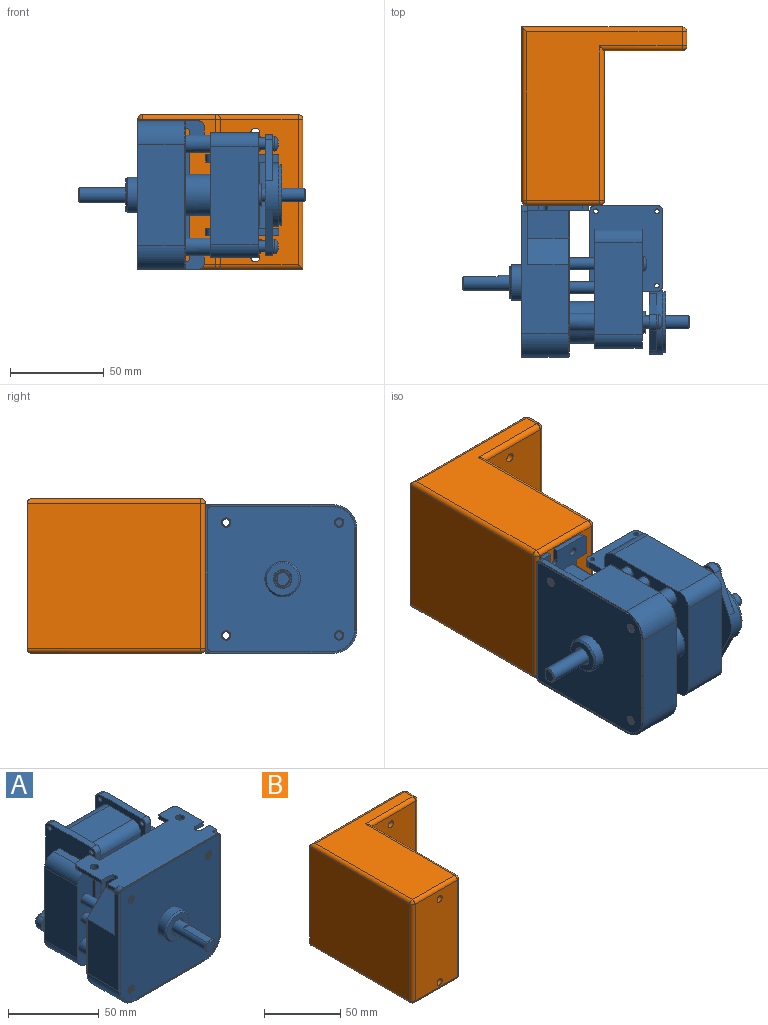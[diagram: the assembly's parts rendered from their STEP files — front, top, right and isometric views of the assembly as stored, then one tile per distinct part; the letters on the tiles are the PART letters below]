
ASSEMBLY  parts=2 mates=1
PART A: 196 faces, bbox 81.7x121.6x82.2 mm
  f0: plane 35.26x18.4mm, normal (0,0,-1), area 648.6mm2, adj f167,f168,f174,f176
  f1: plane 35.26x18.4mm, normal (0,0,1), area 648.6mm2, adj f167,f168,f175,f177
  f2: plane 39.76x3.96mm, normal (0,-1,0), area 157.5mm2, adj f165,f167,f179,f181
  f3: plane 39.69x3.96mm, normal (0,1,0), area 157.3mm2, adj f165,f167,f182,f185
  f4: plane 35.26x25.4mm, normal (0,0,1), area 895.5mm2, adj f6,f106,f167,f168
  f5: plane 78.11x77.78mm, normal (0,1,0), area 4716.9mm2, adj f72,f96,f97,f98,f99,f100,f101,f102
  f6: plane 66.68x63.5mm, normal (0,-1,0), area 2092.8mm2, adj f4,f105,f108,f109,f110,f111,f112,f113
  f7: plane 9.46x2.54mm, normal (0,1,0), area 24mm2, adj f12,f72,f92,f94
  f8: plane 5.54x2.54mm, normal (-1,0,0), area 14.1mm2, adj f12,f72,f78,f88
  f9: plane 5.54x2.54mm, normal (1,0,0), area 14.1mm2, adj f12,f72,f79,f83
  f10: plane 78.66x77.09mm, normal (0,-1,0), area 5641.5mm2, adj f29,f30,f31,f32,f33,f34,f35,f36
  f11: cylinder r=3.17mm len=3.18mm, axis (0,-1,0), area 15.8mm2, adj f12,f18,f19,f75,f78
  f12: plane 79.25x35.56mm, normal (0,0,1), area 2254.7mm2, adj f7,f8,f9,f11,f13,f19,f78,f79
  f13: cylinder r=3.17mm len=3.18mm, axis (0,-1,0), area 15.8mm2, adj f12,f14,f19,f71,f79
  f14: plane 65.08x24.77mm, normal (1,0,0), area 994.6mm2, adj f13,f15,f19,f71,f73,f104
  f15: cylinder r=12.7mm len=24.77mm, axis (0,-1,0), area 494mm2, adj f14,f16,f19,f102
  f16: plane 53.98x24.77mm, normal (0,0,-1), area 1336.7mm2, adj f15,f17,f19,f100
  f17: cylinder r=12.7mm len=24.77mm, axis (0,-1,0), area 494mm2, adj f16,f18,f19,f99
  f18: plane 65.08x24.77mm, normal (-1,0,0), area 994.6mm2, adj f11,f17,f19,f75,f77,f98
  f19: plane 80.95x79.38mm, normal (0,-1,0), area 270.5mm2, adj f11,f12,f13,f14,f15,f16,f17,f18
  f20: cylinder r=2.29mm len=2.29mm, axis (0,-1,0), area 2.7mm2, adj f19,f21,f27,f28
  f21: plane 73.03x0.76mm, normal (0,0,-1), area 55.6mm2, adj f19,f20,f22,f28
  f22: cylinder r=2.29mm len=2.29mm, axis (0,-1,0), area 2.7mm2, adj f19,f21,f23,f28
  f23: plane 65.08x0.76mm, normal (-1,0,0), area 49.6mm2, adj f19,f22,f24,f28
  f24: cylinder r=11.81mm len=11.81mm, axis (0,-1,0), area 14.1mm2, adj f19,f23,f25,f28
  f25: plane 53.98x0.76mm, normal (0,0,1), area 41.1mm2, adj f19,f24,f26,f28
  f26: cylinder r=11.81mm len=11.81mm, axis (0,-1,0), area 14.1mm2, adj f19,f25,f27,f28
  f27: plane 65.08x0.76mm, normal (1,0,0), area 49.6mm2, adj f19,f20,f26,f28
  f28: plane 79.17x77.6mm, normal (0,-1,0), area 76.4mm2, adj f20,f21,f22,f23,f24,f25,f26,f27
  f29: cylinder r=2.03mm len=2.03mm, axis (0,-1,0), area 2.4mm2, adj f10,f28,f30,f36
  f30: plane 73.03x0.76mm, normal (0,0,1), area 55.6mm2, adj f10,f28,f29,f31
  f31: cylinder r=2.03mm len=2.03mm, axis (0,-1,0), area 2.4mm2, adj f10,f28,f30,f32
  f32: plane 65.08x0.76mm, normal (1,0,0), area 49.6mm2, adj f10,f28,f31,f33
  f33: cylinder r=11.56mm len=11.56mm, axis (0,-1,0), area 13.8mm2, adj f10,f28,f32,f34
  f34: plane 53.98x0.76mm, normal (0,0,-1), area 41.1mm2, adj f10,f28,f33,f35
  f35: cylinder r=11.56mm len=11.56mm, axis (0,-1,0), area 13.8mm2, adj f10,f28,f34,f36
  f36: plane 65.08x0.76mm, normal (-1,0,0), area 49.6mm2, adj f10,f28,f29,f35
  f37: cylinder r=9.53mm len=19.05mm, axis (0,1,0), area 326.8mm2, adj f10,f61
  f38: plane 17.27x17.27mm, normal (0,-1,0), area 156.2mm2, adj f61,f65
  f39: cone r=2.5mm half-angle=45deg, axis (0,-1,0), area 6.7mm2, adj f10,f41,f42,f43,f44
  f40: plane 4.62x4.56mm, normal (0,-1,0), area 14.9mm2, adj f41,f42,f43,f44
  f41: cylinder r=2.41mm len=6.26mm, axis (0,-1,0), area 6.6mm2, adj f39,f40,f42,f44
  f42: bspline ~6.76x5.67mm, area 52.2mm2, adj f39,f40,f41,f43
  f43: cylinder r=1.98mm len=5.83mm, axis (0,1,0), area 10.7mm2, adj f39,f40,f42,f44
  f44: bspline ~6.89x5.67mm, area 51.4mm2, adj f39,f40,f41,f43
  f45: cone r=2.5mm half-angle=45deg, axis (0,-1,0), area 6.7mm2, adj f10,f47,f48,f49,f50
  f46: plane 4.62x4.56mm, normal (0,-1,0), area 14.9mm2, adj f47,f48,f49,f50
  f47: cylinder r=2.41mm len=6.26mm, axis (0,-1,0), area 6.6mm2, adj f45,f46,f48,f50
  f48: bspline ~6.76x5.67mm, area 52.2mm2, adj f45,f46,f47,f49
  f49: cylinder r=1.98mm len=5.83mm, axis (0,1,0), area 10.7mm2, adj f45,f46,f48,f50
  f50: bspline ~6.89x5.67mm, area 51.4mm2, adj f45,f46,f47,f49
  f51: cone r=2.5mm half-angle=45deg, axis (0,-1,0), area 6.7mm2, adj f10,f52,f53,f54,f55
  f52: cylinder r=2.41mm len=4.83mm, axis (0,-1,0), area 6.1mm2, adj f51,f53,f55,f75
  f53: bspline ~5.67x4.91mm, area 24.9mm2, adj f51,f52,f54,f75
  f54: cylinder r=1.98mm len=3.97mm, axis (0,1,0), area 8.3mm2, adj f51,f53,f55,f75
  f55: bspline ~5.67x4.91mm, area 24.2mm2, adj f51,f52,f54,f75
  f56: cone r=2.5mm half-angle=45deg, axis (0,-1,0), area 6.7mm2, adj f10,f57,f58,f59,f60
  f57: cylinder r=2.41mm len=4.83mm, axis (0,-1,0), area 6.1mm2, adj f56,f58,f60,f71
  f58: bspline ~5.67x4.91mm, area 24.9mm2, adj f56,f57,f59,f71
  f59: cylinder r=1.98mm len=3.97mm, axis (0,1,0), area 8.3mm2, adj f56,f58,f60,f71
  f60: bspline ~5.67x4.91mm, area 24.2mm2, adj f56,f57,f59,f71
  f61: cone r=8.64mm half-angle=45deg, axis (0,1,0), area 71.7mm2, adj f37,f38
  f62: cylinder r=4.6mm len=9.21mm, axis (0,-1,0), area 33.1mm2, adj f63,f65
  f63: plane 9.21x9.21mm, normal (0,-1,0), area 17.1mm2, adj f62,f64
  f64: cylinder r=3.97mm len=26.42mm, axis (0,-1,0), area 563.9mm2, adj f63,f67,f68,f70
  f65: cone r=4.6mm half-angle=45deg, axis (0,-1,0), area 16.2mm2, adj f38,f62
  f66: plane 6.92x6.13mm, normal (0,-1,0), area 35.2mm2, adj f69,f70
  f67: plane 18.54x4.77mm, normal (0,0,1), area 88.4mm2, adj f64,f68,f69
  f68: plane 4.77x0.8mm, normal (0,-1,0), area 2.6mm2, adj f64,f67
  f69: plane 4.78x0.52mm, normal (0,-0.71,0.71), area 3.3mm2, adj f66,f67,f70
  f70: cone r=3.46mm half-angle=45deg, axis (0,1,0), area 13.2mm2, adj f64,f66,f69
  f71: plane 29.43x14.51mm, normal (0,1,0), area 300.4mm2, adj f13,f14,f57,f58,f59,f60,f72,f73
  f72: plane 79.25x32.39mm, normal (0,0,-1), area 894mm2, adj f5,f7,f8,f9,f71,f74,f75,f76
  f73: plane 21.59x14.29mm, normal (0.71,0,0.71), area 436.2mm2, adj f14,f71,f74,f103
  f74: plane 21.59x14.92mm, normal (1,0,0), area 322.2mm2, adj f71,f72,f73,f101
  f75: plane 29.43x14.51mm, normal (0,1,0), area 300.4mm2, adj f11,f18,f52,f53,f54,f55,f72,f76
  f76: plane 21.59x14.92mm, normal (-1,0,0), area 322.2mm2, adj f72,f75,f77,f96
  f77: plane 21.59x14.29mm, normal (-0.71,0,0.71), area 436.2mm2, adj f18,f75,f76,f97
  f78: plane 3.11x2.54mm, normal (0,-1,0), area 2mm2, adj f8,f11,f12
  f79: plane 3.11x2.54mm, normal (0,-1,0), area 2mm2, adj f9,f12,f13
  f80: plane 18.9x2.54mm, normal (1,0,0), area 48mm2, adj f12,f72,f85,f94
  f81: plane 18.9x2.54mm, normal (-1,0,0), area 48mm2, adj f12,f72,f89,f95
  f82: plane 9.46x2.54mm, normal (0,1,0), area 24mm2, adj f12,f72,f93,f95
  f83: plane 6.29x2.54mm, normal (0,1,0), area 16mm2, adj f9,f12,f72,f84
  f84: cylinder r=2.38mm len=4.76mm, axis (0,0,1), area 19mm2, adj f12,f72,f83,f85
  f85: plane 6.29x2.54mm, normal (0,-1,0), area 16mm2, adj f12,f72,f80,f84
  f86: cylinder r=2.41mm len=4.83mm, axis (0,0,1), area 38.5mm2, adj f12,f72
  f87: cylinder r=2.38mm len=4.76mm, axis (0,0,1), area 19mm2, adj f12,f72,f88,f89
  f88: plane 6.29x2.54mm, normal (0,1,0), area 16mm2, adj f8,f12,f72,f87
  f89: plane 6.29x2.54mm, normal (0,-1,0), area 16mm2, adj f12,f72,f81,f87
  f90: cylinder r=2.41mm len=4.83mm, axis (0,0,1), area 38.5mm2, adj f12,f72
  f91: plane 53.98x2.54mm, normal (0,1,0), area 137.1mm2, adj f12,f72,f92,f93
  f92: plane 7.87x2.54mm, normal (-1,0,0), area 20mm2, adj f7,f12,f72,f91
  f93: plane 7.87x2.54mm, normal (1,0,0), area 20mm2, adj f12,f72,f82,f91
  f94: cylinder r=3.17mm len=3.18mm, axis (0,0,-1), area 12.7mm2, adj f7,f12,f72,f80
  f95: cylinder r=3.17mm len=3.18mm, axis (0,0,1), area 12.7mm2, adj f12,f72,f81,f82
  f96: cylinder r=0.64mm len=15.19mm, axis (0,0,-1), area 15mm2, adj f5,f72,f76,f97
  f97: cylinder r=0.64mm len=14.92mm, axis (-0.71,0,-0.71), area 20.2mm2, adj f5,f77,f96,f98
  f98: cylinder r=0.64mm len=36.5mm, axis (0,0,1), area 36.3mm2, adj f5,f18,f97,f99
  f99: torus R=12.06mm, axis (0,-1,0), area 19.5mm2, adj f5,f17,f98,f100
  f100: cylinder r=0.64mm len=53.98mm, axis (-1,0,0), area 53.8mm2, adj f5,f16,f99,f102
  f101: cylinder r=0.64mm len=15.19mm, axis (0,0,1), area 15mm2, adj f5,f72,f74,f103
  f102: torus R=12.06mm, axis (0,-1,0), area 19.5mm2, adj f5,f15,f100,f104
  f103: cylinder r=0.64mm len=14.92mm, axis (-0.71,0,0.71), area 20.2mm2, adj f5,f73,f101,f104
  f104: cylinder r=0.64mm len=36.5mm, axis (0,0,-1), area 36.3mm2, adj f5,f14,f102,f103
  f105: cylinder r=11.11mm len=22.23mm, axis (0,1,0), area 939.9mm2, adj f5,f6
  f106: plane 66.68x63.5mm, normal (0,1,0), area 2425.6mm2, adj f4,f108,f109,f110,f111,f112,f113,f114
  f107: plane 64.45x34.01mm, normal (0,-1,0), area 1284.3mm2, adj f117,f120,f121,f122,f123,f124,f125,f129
  f108: cylinder r=7.15mm len=25.4mm, axis (0,-1,0), area 285.3mm2, adj f6,f106,f109,f116
  f109: plane 49.2x25.4mm, normal (1,0,0), area 1249.7mm2, adj f6,f106,f108,f110
  f110: cylinder r=7.15mm len=25.4mm, axis (0,-1,0), area 285.3mm2, adj f6,f106,f109,f111
  f111: plane 52.38x25.4mm, normal (0,0,-1), area 1330.3mm2, adj f6,f106,f110,f112
  f112: cylinder r=7.15mm len=25.4mm, axis (0,-1,0), area 285.3mm2, adj f6,f106,f111,f113
  f113: plane 49.2x25.4mm, normal (-1,0,0), area 1249.7mm2, adj f6,f106,f112,f114
  f114: cylinder r=7.15mm len=25.4mm, axis (0,-1,0), area 285.3mm2, adj f6,f106,f113,f115
  f115: plane 25.4x4.6mm, normal (0,0,1), area 116.8mm2, adj f6,f106,f114,f163
  f116: plane 25.4x4.6mm, normal (0,0,1), area 116.8mm2, adj f6,f106,f108,f165
  f117: cylinder r=3.17mm len=6.35mm, axis (0,-1,0), area 76mm2, adj f106,f107
  f118: plane 30.44x24.65mm, normal (0,1,0), area 190.2mm2, adj f120,f121,f122,f129,f138
  f119: plane 30.44x24.65mm, normal (0,1,0), area 190.2mm2, adj f123,f124,f125,f129,f136
  f120: plane 22.01x10.96mm, normal (0.45,0,0.9), area 101.5mm2, adj f107,f118,f121,f129
  f121: cylinder r=4.76mm len=8.53mm, axis (0,1,0), area 43.6mm2, adj f107,f118,f120,f122
  f122: plane 22.01x10.96mm, normal (0.45,0,-0.9), area 101.5mm2, adj f107,f118,f121,f129
  f123: plane 22.01x10.96mm, normal (-0.45,0,0.9), area 101.5mm2, adj f107,f119,f125,f129
  f124: plane 22.01x10.96mm, normal (-0.45,0,-0.9), area 101.5mm2, adj f107,f119,f125,f129
  f125: cylinder r=4.76mm len=8.53mm, axis (0,1,0), area 43.6mm2, adj f107,f119,f123,f124
  f126: plane 32.39x32.39mm, normal (0,1,0), area 764.6mm2, adj f128,f135
  f127: plane 34.01x34.01mm, normal (0,1,0), area 84.8mm2, adj f128,f129
  f128: cylinder r=16.19mm len=32.39mm, axis (0,1,0), area 161.5mm2, adj f126,f127
  f129: cylinder r=17.01mm len=34.01mm, axis (0,1,0), area 469mm2, adj f107,f118,f119,f120,f122,f123,f124,f127
  f130: cylinder r=3.83mm len=7.66mm, axis (0,1,0), area 64.2mm2, adj f131,f135
  f131: plane 7.66x7.66mm, normal (0,1,0), area 5.9mm2, adj f130,f134
  f132: plane 6.13x6.13mm, normal (0,1,0), area 29.6mm2, adj f133
  f133: cone r=3.58mm half-angle=45deg, axis (0,-1,0), area 15mm2, adj f132,f134
  f134: cylinder r=3.58mm len=15.37mm, axis (0,1,0), area 345.2mm2, adj f131,f133
  f135: cone r=3.83mm half-angle=45deg, axis (0,1,0), area 18.4mm2, adj f126,f130
  f136: cylinder r=3.97mm len=7.94mm, axis (0,-1,0), area 19.8mm2, adj f119,f137
  f137: revolved ~7.94x7.94mm, area 70.7mm2, adj f136
  f138: cylinder r=3.97mm len=7.94mm, axis (0,-1,0), area 19.8mm2, adj f118,f139
  f139: revolved ~7.94x7.94mm, area 70.7mm2, adj f138
  f140: cylinder r=3.17mm len=6.35mm, axis (0,-1,0), area 76mm2, adj f106,f107
  f141: cylinder r=3.58mm len=7.15mm, axis (0,-1,0), area 49.9mm2, adj f107,f142
  f142: plane 11.98x11.98mm, normal (0,1,0), area 72.5mm2, adj f141,f143
  f143: cylinder r=5.99mm len=11.98mm, axis (0,-1,0), area 59.7mm2, adj f106,f142
  f144: cylinder r=1.98mm len=3.96mm, axis (0,1,0), area 11.1mm2, adj f106,f145
  f145: plane 3.96x3.96mm, normal (0,1,0), area 12.3mm2, adj f144
  f146: cylinder r=1.98mm len=3.96mm, axis (0,1,0), area 11.1mm2, adj f106,f147
  f147: plane 3.96x3.96mm, normal (0,1,0), area 12.3mm2, adj f146
  f148: cylinder r=1.98mm len=3.96mm, axis (0,1,0), area 11.1mm2, adj f106,f149
  f149: plane 3.96x3.96mm, normal (0,1,0), area 12.3mm2, adj f148
  f150: cylinder r=1.98mm len=3.96mm, axis (0,1,0), area 11.1mm2, adj f106,f151
  f151: plane 3.96x3.96mm, normal (0,1,0), area 12.3mm2, adj f150
  f152: cylinder r=3.97mm len=7.94mm, axis (0,-1,0), area 15.8mm2, adj f106,f153
  f153: revolved ~7.94x7.94mm, area 67.2mm2, adj f152
  f154: cylinder r=3.97mm len=7.94mm, axis (0,-1,0), area 15.8mm2, adj f106,f155
  f155: revolved ~7.94x7.94mm, area 67.2mm2, adj f154
  f156: cylinder r=3.17mm len=13.46mm, axis (0,1,0), area 268.6mm2, adj f5,f6
  f157: cylinder r=3.17mm len=13.46mm, axis (0,1,0), area 268.6mm2, adj f5,f6
  f158: cylinder r=4.76mm len=13.46mm, axis (0,1,0), area 402.8mm2, adj f5,f6
  f159: cylinder r=4.76mm len=13.46mm, axis (0,1,0), area 402.8mm2, adj f5,f6
  f160: cylinder r=3.17mm len=13.46mm, axis (0,1,0), area 268.6mm2, adj f5,f6
  f161: cylinder r=3.17mm len=13.46mm, axis (0,1,0), area 268.6mm2, adj f5,f6
  f162: plane 7.94x3.96mm, normal (0,0,-1), area 31.5mm2, adj f106,f163,f168,f183
  f163: plane 46.04x39.02mm, normal (-1,0,0), area 924.7mm2, adj f6,f106,f115,f162,f169,f170,f171,f178
  f164: plane 7.94x3.96mm, normal (0,0,-1), area 31.5mm2, adj f106,f165,f167,f182
  f165: plane 46.04x39.02mm, normal (1,0,0), area 924.7mm2, adj f2,f3,f6,f106,f116,f164,f166,f179
  f166: plane 32.67x3.96mm, normal (0,0,1), area 129.5mm2, adj f165,f167,f181,f185
  f167: plane 46.04x39.02mm, normal (-1,0,0), area 617.2mm2, adj f0,f1,f2,f3,f4,f164,f166,f172
  f168: plane 46.04x39.02mm, normal (1,0,0), area 617.2mm2, adj f0,f1,f4,f162,f169,f170,f171,f172
  f169: plane 32.67x3.96mm, normal (0,0,1), area 129.5mm2, adj f163,f168,f180,f184
  f170: plane 39.76x3.96mm, normal (0,-1,0), area 157.5mm2, adj f163,f168,f178,f180
  f171: plane 39.69x3.96mm, normal (0,1,0), area 157.3mm2, adj f163,f168,f183,f184
  f172: plane 35.26x25.41mm, normal (0,1,0), area 895.9mm2, adj f167,f168,f176,f177
  f173: plane 35.26x25.41mm, normal (0,-1,0), area 895.9mm2, adj f167,f168,f174,f175
  f174: cylinder r=6.35mm len=35.26mm, axis (-1,0,0), area 351.7mm2, adj f0,f167,f168,f173
  f175: cylinder r=6.35mm len=35.26mm, axis (1,0,0), area 351.7mm2, adj f1,f167,f168,f173
  f176: cylinder r=6.35mm len=35.26mm, axis (1,0,0), area 351.7mm2, adj f0,f167,f168,f172
  f177: cylinder r=6.35mm len=35.26mm, axis (-1,0,0), area 351.7mm2, adj f1,f167,f168,f172
  f178: cylinder r=3.17mm len=3.96mm, axis (-1,0,0), area 17.1mm2, adj f6,f163,f168,f170
  f179: cylinder r=3.17mm len=3.96mm, axis (-1,0,0), area 17.1mm2, adj f2,f6,f165,f167
  f180: cylinder r=3.17mm len=3.96mm, axis (-1,0,0), area 19.8mm2, adj f163,f168,f169,f170
  f181: cylinder r=3.17mm len=3.96mm, axis (-1,0,0), area 19.8mm2, adj f2,f165,f166,f167
  f182: cylinder r=3.17mm len=3.96mm, axis (1,0,0), area 19.8mm2, adj f3,f164,f165,f167
  f183: cylinder r=3.17mm len=3.96mm, axis (1,0,0), area 19.8mm2, adj f162,f163,f168,f171
  f184: cylinder r=3.17mm len=3.96mm, axis (-1,0,0), area 19.8mm2, adj f163,f168,f169,f171
  f185: cylinder r=3.17mm len=3.96mm, axis (-1,0,0), area 19.8mm2, adj f3,f165,f166,f167
  f186: cylinder r=1.27mm len=3.96mm, axis (-1,0,0), area 31.6mm2, adj f163,f168
  f187: cylinder r=1.27mm len=3.96mm, axis (-1,0,0), area 31.6mm2, adj f165,f167
  f188: cylinder r=1.27mm len=3.96mm, axis (-1,0,0), area 31.6mm2, adj f163,f168,f189
  f189: plane 2.54x1.94mm, normal (1,0,0), area 4.1mm2, adj f6,f188
  f190: plane 2.54x1.94mm, normal (-1,0,0), area 4.1mm2, adj f6,f191
  f191: cylinder r=1.27mm len=3.96mm, axis (-1,0,0), area 31.6mm2, adj f165,f167,f190
  f192: cylinder r=1.27mm len=3.96mm, axis (-1,0,0), area 31.6mm2, adj f163,f168
  f193: cylinder r=1.27mm len=3.96mm, axis (-1,0,0), area 31.6mm2, adj f165,f167
  f194: cylinder r=1.27mm len=3.96mm, axis (-1,0,0), area 31.6mm2, adj f163,f168
  f195: cylinder r=1.27mm len=3.96mm, axis (-1,0,0), area 31.6mm2, adj f165,f167
PART B: 35 faces, bbox 88.2x95.3x82.6 mm
  f0: plane 85.67x77.47mm, normal (0,1,0), area 6600.6mm2, adj f5,f8,f9,f12,f33,f34
  f1: plane 77.47x41.57mm, normal (0,-1,0), area 3183.6mm2, adj f7,f14,f23,f26,f33,f34
  f2: plane 77.47x39.03mm, normal (0,-1,0), area 2986.8mm2, adj f17,f18,f24,f25,f29,f31
  f3: plane 90.17x83.13mm, normal (0,0,1), area 3855.2mm2, adj f8,f10,f14,f15,f18,f19
  f4: plane 80.01x7.62mm, normal (1,0,0), area 609.7mm2, adj f6,f9,f15,f23
  f5: plane 92.71x77.47mm, normal (-1,0,0), area 7182.2mm2, adj f0,f10,f16,f17
  f6: plane 90.17x85.67mm, normal (0,0,-1), area 3874.5mm2, adj f4,f12,f16,f24,f26,f28
  f7: plane 80.01x77.47mm, normal (1,0,0), area 6198.4mm2, adj f1,f19,f25,f28
  f8: cylinder r=2.54mm len=85.67mm, axis (-1,0,0), area 338.1mm2, adj f0,f3,f10,f11
  f9: cylinder r=2.54mm len=80.01mm, axis (0,0,1), area 315.5mm2, adj f0,f4,f11,f12
  f10: cylinder r=2.54mm len=92.71mm, axis (0,1,0), area 366.2mm2, adj f3,f5,f8,f13
  f11: sphere r=2.54mm, area 10.1mm2, adj f8,f9,f15
  f12: cylinder r=2.54mm len=88.21mm, axis (1,0,0), area 344.6mm2, adj f0,f6,f9,f16
  f13: sphere r=2.54mm, area 10.1mm2, adj f10,f17,f18
  f14: cylinder r=2.54mm len=44.11mm, axis (1,0,0), area 169.5mm2, adj f1,f3,f19,f20
  f15: cylinder r=2.54mm len=7.62mm, axis (0,-1,0), area 30.4mm2, adj f3,f4,f11,f20
  f16: cylinder r=2.54mm len=92.71mm, axis (0,-1,0), area 366.2mm2, adj f5,f6,f12,f21
  f17: cylinder r=2.54mm len=77.47mm, axis (0,0,1), area 309.1mm2, adj f2,f5,f13,f21
  f18: cylinder r=2.54mm len=39.03mm, axis (1,0,0), area 155.7mm2, adj f2,f3,f13,f22
  f19: cylinder r=2.54mm len=82.55mm, axis (0,-1,0), area 322.9mm2, adj f3,f7,f14,f22
  f20: sphere r=2.54mm, area 10.1mm2, adj f14,f15,f23
  f21: sphere r=2.54mm, area 10.1mm2, adj f16,f17,f24
  f22: sphere r=2.54mm, area 10.1mm2, adj f18,f19,f25
  f23: cylinder r=2.54mm len=80.01mm, axis (0,0,-1), area 315.5mm2, adj f1,f4,f20,f26
  f24: cylinder r=2.54mm len=39.03mm, axis (-1,0,0), area 155.7mm2, adj f2,f6,f21,f27
  f25: cylinder r=2.54mm len=77.47mm, axis (0,0,1), area 309.1mm2, adj f2,f7,f22,f27
  f26: cylinder r=2.54mm len=46.65mm, axis (-1,0,0), area 176mm2, adj f1,f6,f23,f28
  f27: sphere r=2.54mm, area 10.1mm2, adj f24,f25,f28
  f28: cylinder r=2.54mm len=82.55mm, axis (0,1,0), area 322.9mm2, adj f6,f7,f26,f27
  f29: cylinder r=2.41mm len=19.05mm, axis (0,-1,0), area 288.8mm2, adj f2,f30
  f30: plane 4.83x4.83mm, normal (0,-1,0), area 18.3mm2, adj f29
  f31: cylinder r=2.41mm len=19.05mm, axis (0,-1,0), area 288.8mm2, adj f2,f32
  f32: plane 4.83x4.83mm, normal (0,-1,0), area 18.3mm2, adj f31
  f33: cylinder r=2.41mm len=12.7mm, axis (0,-1,0), area 192.5mm2, adj f0,f1
  f34: cylinder r=2.41mm len=12.7mm, axis (0,-1,0), area 192.5mm2, adj f0,f1
PLACE A rot(axis=(-0.58,-0.58,-0.58),120deg) t=(-42.71,-80.42,6.28)mm
PLACE B t=(-42.71,50.55,-33.34)mm
MATE fastened A.f86 <-> B.f29  axis (0,1,0) through (-17.31,-44.7,39.62)mm
